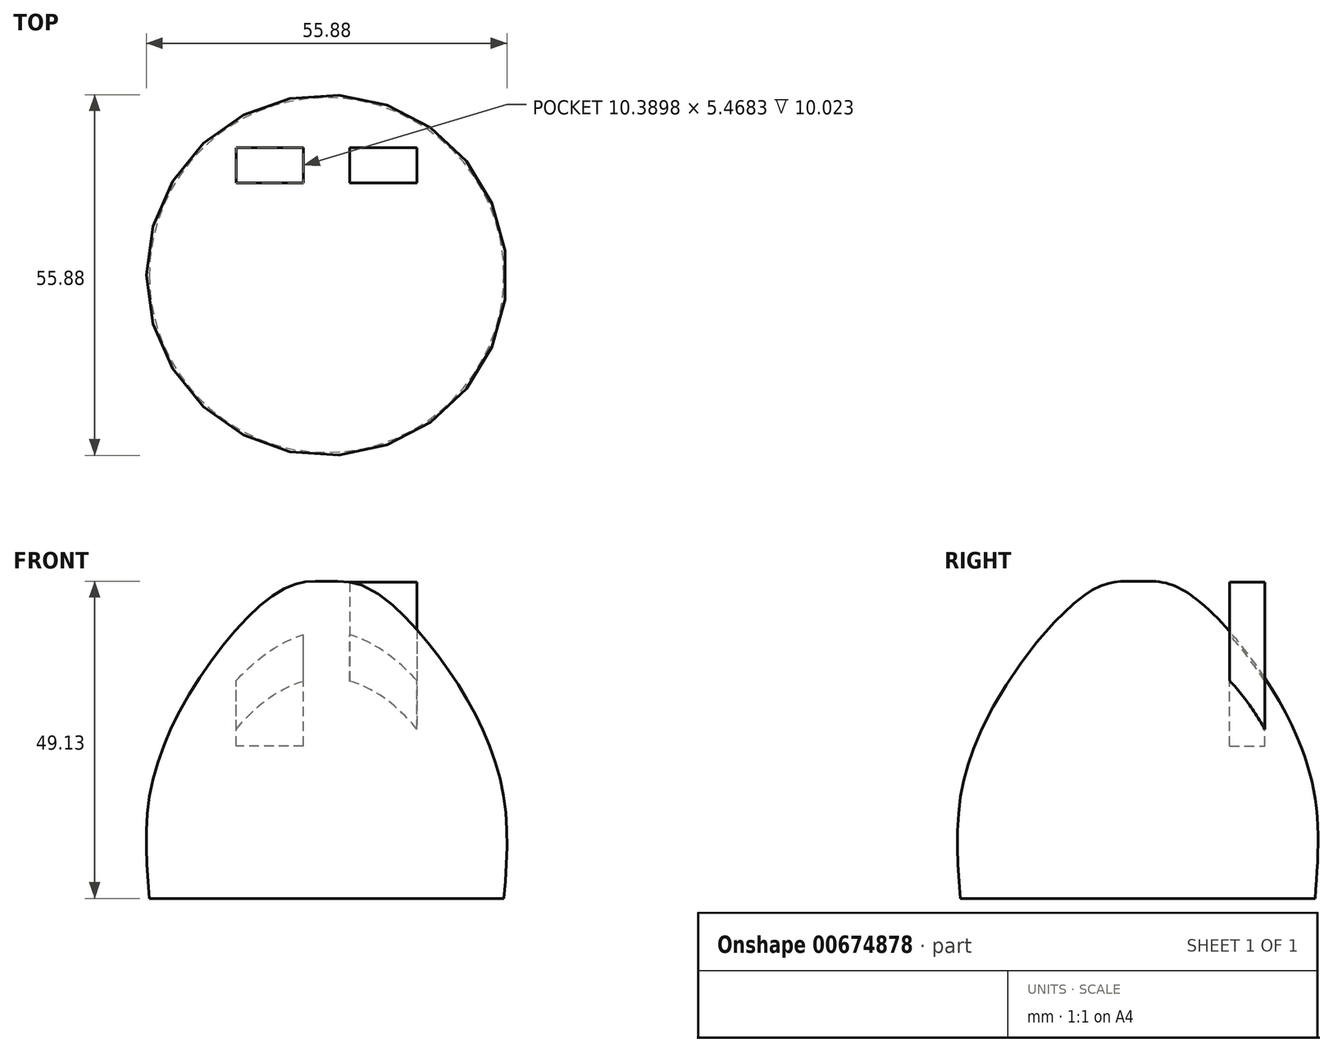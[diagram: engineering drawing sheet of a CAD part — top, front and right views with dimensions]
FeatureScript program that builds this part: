
annotation { "Feature Type Name" : "Feature", "Feature Type Description" : "" }
export const myFeature = defineFeature(function(context is Context, id is Id, definition is map)
    precondition{}
    {
        {
            var Q0;
            Q0=qCreatedBy(makeId("Front.planeOp"),FACE);
            var sketch = newSketch(context, id + "F0", { "sketchPlane" : qUnion([Q0])});
            skLineSegment(sketch, "E0", {"start": v(0, 38.42) * mm, "end": v(0, -34.4) * mm});
            skFitSpline(sketch, "E1", {"points": [v(-27.49, 0) * mm, v(-27.2, 17.12) * mm, v(-18.56, 35.83) * mm, v(-6.19, 48.2) * mm, v(0, 49.07) * mm], "startDerivative": vector(-4.83, 63.24) * mm, "endDerivative": vector(36.05, -1.93) * mm});
            skLineSegment(sketch, "E2", {"start": v(-27.49, 0) * mm, "end": v(0, 0) * mm});
            skLineSegment(sketch, "E3", {"start": v(0, 0) * mm, "end": v(0, 49.07) * mm});
            skSolve(sketch);
        }
        {
            var Q0;
            {var subQ0=sQuery(id+"F0.wireOp",EDGE,"E1");Q0=makeQuery(id+"F0.imprint","IMPRINT",FACE,{"disambiguationData":[TD([[makeQuery(id+"F0.imprint","IMPRINT",EDGE,{"derivedFrom":subQ0}),-1.0]])]});}
            var Q1;
            Q1=sQuery(id+"F0.wireOp",EDGE,"E0");
            revolve(context, id + "F1", {"entities" : qUnion([Q0]), "axis" : qUnion([Q1]), "revolveType" : RevolveType.FULL});
        }
        {
            var Q0;
            Q0=qCreatedBy(makeId("Top.planeOp"),FACE);
            cPlane(context, id + "F2", {"entities" : qUnion([Q0]), "cplaneType" : CPlaneType.OFFSET, "offset" : 76.2 * mm, "width" : 152.4 * mm, "height" : 152.4 * mm});
        }
        {
            var Q0;
            Q0=qCreatedBy(id+"F2.planeOp",FACE);
            var sketch = newSketch(context, id + "F3", { "sketchPlane" : qUnion([Q0])});
            skLineSegment(sketch, "E4.bottom", {"start": v(-3.6, 14.25) * mm, "end": v(-13.99, 14.25) * mm});
            skLineSegment(sketch, "E4.top", {"start": v(-3.6, 19.71) * mm, "end": v(-13.99, 19.71) * mm});
            skLineSegment(sketch, "E4.left", {"start": v(-3.6, 14.25) * mm, "end": v(-3.6, 19.71) * mm});
            skLineSegment(sketch, "E4.right", {"start": v(-13.99, 14.25) * mm, "end": v(-13.99, 19.71) * mm});
            skPoint(sketch, "E4.middle", {"position": v(-8.8, 16.98) * mm});
            skLineSegment(sketch, "E5", {"start": v(0, 46.77) * mm, "end": v(0, -35.54) * mm});
            skPoint(sketch, "E6.MirrorP", {"position": v(8.8, 16.98) * mm});
            skLineSegment(sketch, "E7.MirrorCS", {"start": v(13.99, 14.25) * mm, "end": v(13.99, 19.71) * mm});
            skLineSegment(sketch, "E8.MirrorCS", {"start": v(3.6, 14.25) * mm, "end": v(3.6, 19.71) * mm});
            skLineSegment(sketch, "E9.MirrorCS", {"start": v(3.6, 19.71) * mm, "end": v(13.99, 19.71) * mm});
            skLineSegment(sketch, "E10.MirrorCS", {"start": v(3.6, 14.25) * mm, "end": v(13.99, 14.25) * mm});
            skSolve(sketch);
        }
        {
            var Q0;
            Q0=makeQuery(id+"F3.imprint","IMPRINT",FACE,{"disambiguationData":[TD([[makeQuery(id+"F3.imprint","IMPRINT",EDGE,{"derivedFrom":sQuery(id+"F3.wireOp",EDGE,"E4.bottom")}),-1.0]])]});
            var Q1;
            Q1=makeQuery(id+"F3.imprint","IMPRINT",FACE,{"disambiguationData":[TD([[makeQuery(id+"F3.imprint","IMPRINT",EDGE,{"derivedFrom":sQuery(id+"F3.wireOp",EDGE,"E7.MirrorCS")}),1.0]])]});
            extrude(context, id + "F4", {"entities" : qUnion([Q0, Q1]), "operationType" : NewBodyOperationType.REMOVE, "oppositeDirection" : true, "depth" : 52.58 * mm, "offsetDistance" : 25.4 * mm});
        }
        {
            var Q0;
            Q0=makeQuery(id+"F4.boolean.opBoolean","COPY",FACE,{"derivedFrom":makeQuery(id+"F4.opExtrude","CAP_FACE",FACE,{"disambiguationData":[OSD([sQuery(id+"F3.wireOp",EDGE,"E7.MirrorCS"),sQuery(id+"F3.wireOp",EDGE,"E8.MirrorCS"),sQuery(id+"F3.wireOp",EDGE,"E9.MirrorCS"),sQuery(id+"F3.wireOp",EDGE,"E10.MirrorCS")])],"isStart":false})});
            extrude(context, id + "F5", {"entities" : qUnion([Q0]), "operationType" : NewBodyOperationType.ADD, "depth" : 25.4 * mm, "offsetDistance" : 25.4 * mm});
        }
    });
